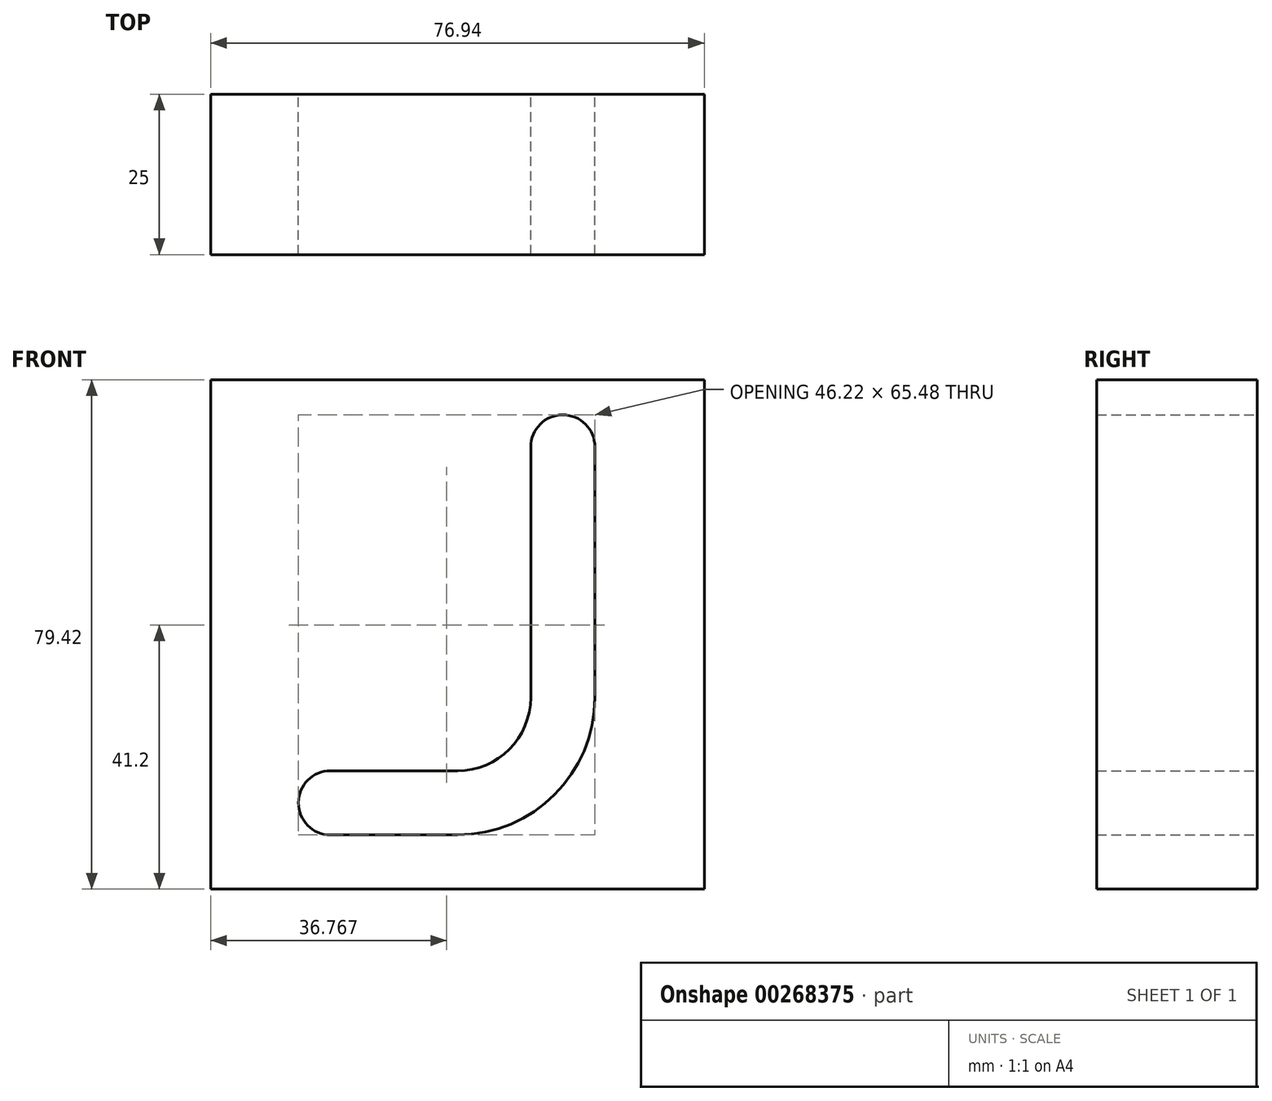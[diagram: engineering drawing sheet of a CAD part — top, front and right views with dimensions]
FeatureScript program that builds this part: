
annotation { "Feature Type Name" : "Feature", "Feature Type Description" : "" }
export const myFeature = defineFeature(function(context is Context, id is Id, definition is map)
    precondition{}
    {
        {
            var Q0;
            Q0=qCreatedBy(makeId("Front.planeOp"),FACE);
            var sketch = newSketch(context, id + "F0", { "sketchPlane" : qUnion([Q0])});
            skLineSegment(sketch, "E0.bottom", {"start": v(38.47, 39.71) * mm, "end": v(-38.47, 39.71) * mm});
            skLineSegment(sketch, "E0.top", {"start": v(38.47, -39.71) * mm, "end": v(-38.47, -39.71) * mm});
            skLineSegment(sketch, "E0.left", {"start": v(38.47, 39.71) * mm, "end": v(38.47, -39.71) * mm});
            skLineSegment(sketch, "E0.right", {"start": v(-38.47, 39.71) * mm, "end": v(-38.47, -39.71) * mm});
            skPoint(sketch, "E0.middle", {"position": v(0, 0) * mm});
            skLineSegment(sketch, "E1.left", {"start": v(11.4, 29.23) * mm, "end": v(11.4, -9.84) * mm});
            skLineSegment(sketch, "E1.right", {"start": v(21.4, 29.23) * mm, "end": v(21.4, -9.84) * mm});
            skLineSegment(sketch, "E2.bottom", {"start": v(0, -31.25) * mm, "end": v(-19.81, -31.25) * mm});
            skLineSegment(sketch, "E2.top", {"start": v(0, -21.25) * mm, "end": v(-19.81, -21.25) * mm});
            skArc(sketch, "E3", {"start": v(-19.81, -31.25) * mm, "mid": v(-24.81, -26.25) * mm, "end": v(-19.81, -21.25) * mm});
            skArc(sketch, "E4", {"start": v(11.4, 29.23) * mm, "mid": v(16.4, 34.23) * mm, "end": v(21.4, 29.23) * mm});
            skArc(sketch, "E5", {"start": v(0, -21.25) * mm, "mid": v(8.06, -17.9) * mm, "end": v(11.4, -9.84) * mm});
            skArc(sketch, "E6", {"start": v(0, -31.25) * mm, "mid": v(15.14, -24.98) * mm, "end": v(21.4, -9.84) * mm});
            skPoint(sketch, "E7.27.internal.snap0", {"position": v(8.06, -17.9) * mm});
            skPoint(sketch, "E7.38.internal.snap0", {"position": v(8.06, -17.9) * mm});
            skSolve(sketch);
        }
        {
            var Q0;
            Q0=makeQuery(id+"F0.imprint","IMPRINT",FACE,{"disambiguationData":[TD([[makeQuery(id+"F0.imprint","IMPRINT",EDGE,{"derivedFrom":sQuery(id+"F0.wireOp",EDGE,"E0.bottom")}),1.0]])]});
            extrude(context, id + "F1", {"entities" : qUnion([Q0]), "depth" : 25 * mm});
        }
    });
